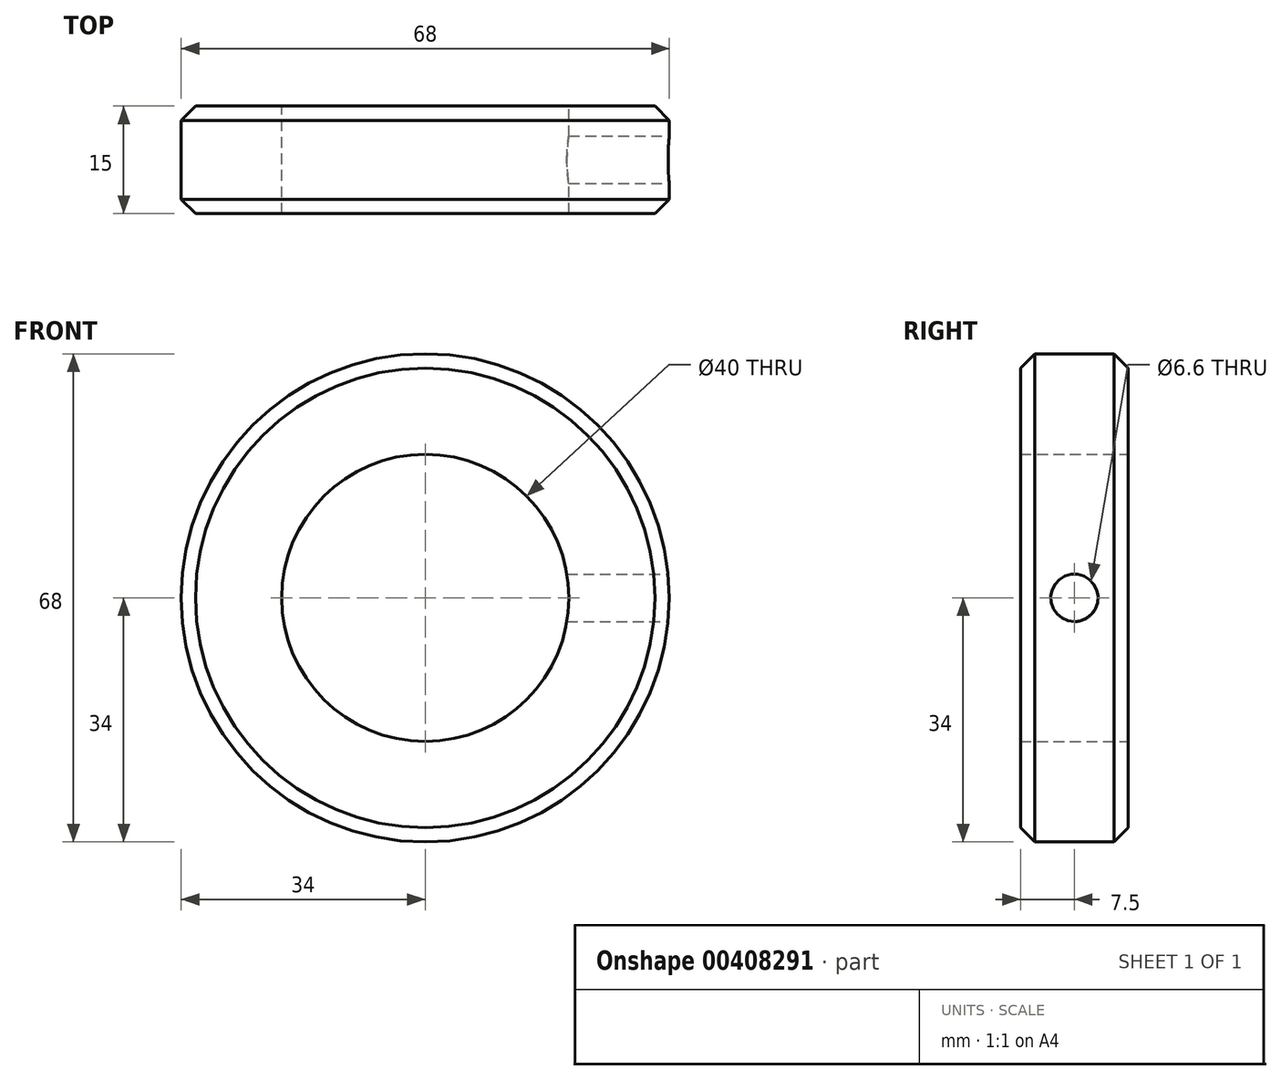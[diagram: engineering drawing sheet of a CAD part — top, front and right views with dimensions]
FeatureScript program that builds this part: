
annotation { "Feature Type Name" : "Feature", "Feature Type Description" : "" }
export const myFeature = defineFeature(function(context is Context, id is Id, definition is map)
    precondition{}
    {
        {
            var Q0;
            Q0=qCreatedBy(makeId("Front.planeOp"),FACE);
            var sketch = newSketch(context, id + "F0", { "sketchPlane" : qUnion([Q0])});
            skCircle(sketch, "E0", {"center": v(0, 0) * mm, "radius": 34 * mm});
            skCircle(sketch, "E1", {"center": v(0, 0) * mm, "radius": 20 * mm});
            skSolve(sketch);
        }
        {
            var Q0;
            Q0 = qSketchRegion(id + "F0", true);
            extrude(context, id + "F1", {"entities" : qUnion([Q0]), "depth" : 15 * mm});
        }
        {
            var Q0;
            Q0=makeQuery(id+"F1.opExtrude","CAP_EDGE",EDGE,{"disambiguationData":[OSD([sQuery(id+"F0.wireOp",EDGE,"E0")])],"isStart":true});
            var Q1;
            Q1=makeQuery(id+"F1.opExtrude","CAP_EDGE",EDGE,{"disambiguationData":[OSD([sQuery(id+"F0.wireOp",EDGE,"E0")])],"isStart":false});
            chamfer(context, id + "F2", {"entities" : qUnion([Q0, Q1]), "width" : 2 * mm, "tangentPropagation" : true});
        }
        {
            var Q0;
            Q0=qCreatedBy(makeId("Right.planeOp"),FACE);
            cPlane(context, id + "F3", {"entities" : qUnion([Q0]), "cplaneType" : CPlaneType.OFFSET, "offset" : 34 * mm, "width" : 150 * mm, "height" : 150 * mm});
        }
        {
            var Q0;
            Q0=qCreatedBy(id+"F3.planeOp",FACE);
            var sketch = newSketch(context, id + "F4", { "sketchPlane" : qUnion([Q0])});
            skPoint(sketch, "E2", {"position": v(-7.5, 0) * mm});
            skSolve(sketch);
        }
        {
            var Q0;
            Q0=sQuery(id+"F4.wireOp",VERTEX,"E2");
            var Q1;
            Q1=makeQuery(id+"F1.opExtrude","SWEPT_BODY",BODY,{"disambiguationData":[OSD([sQuery(id+"F0.wireOp",EDGE,"E0"),sQuery(id+"F0.wireOp",EDGE,"E1")])]});
            hole(context, id + "F5", {"style" : HoleStyle.SIMPLE, "endStyle" : HoleEndStyle.BLIND, "standardTappedOrClearance" : lookupTablePath({ "standard" : "ISO", "fit" : "Normal", "size" : "M6", "type" : "Clearance" }), "standardBlindInLast" : lookupTablePath({ "standard" : "ISO", "fit" : "Standard", "size" : "M6", "type" : "Clearance" }), "holeDiameter" : 6.6 * mm, "holeDepth" : 15 * mm, "isTappedThrough" : true, "tappedDepth" : 12 * mm, "tapClearance" : 3, "locations" : qUnion([Q0]), "scope" : qUnion([Q1])});
        }
    });
